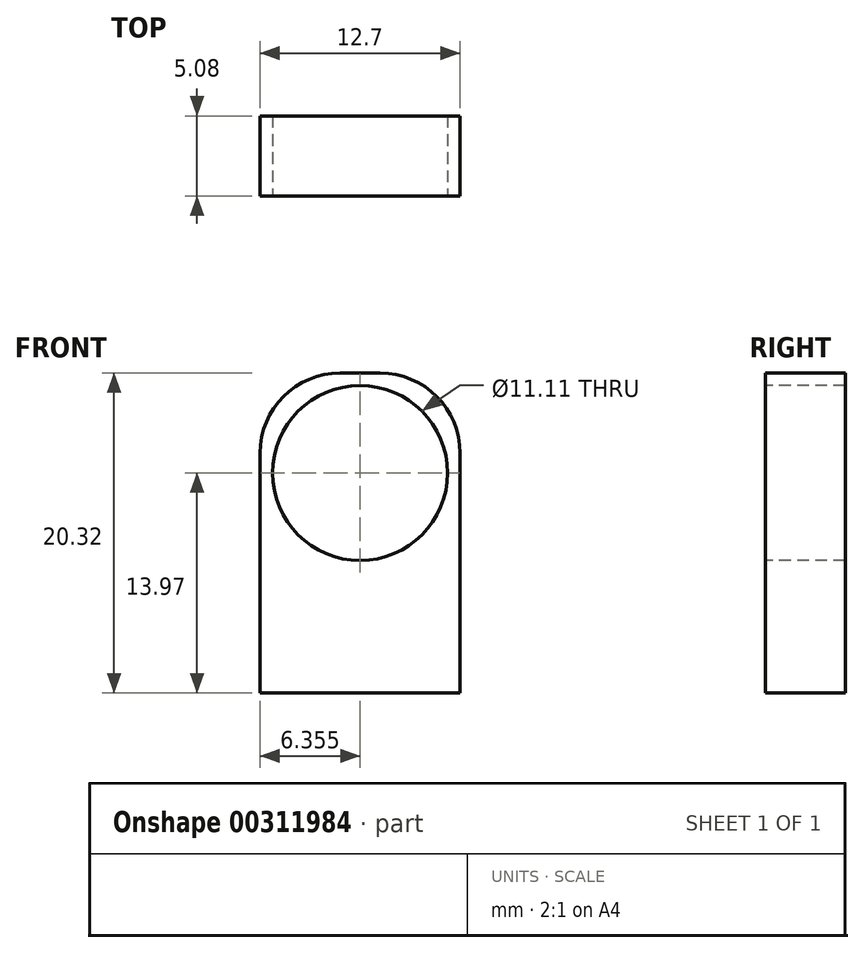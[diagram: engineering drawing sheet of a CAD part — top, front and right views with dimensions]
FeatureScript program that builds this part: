
annotation { "Feature Type Name" : "Feature", "Feature Type Description" : "" }
export const myFeature = defineFeature(function(context is Context, id is Id, definition is map)
    precondition{}
    {
        {
            var Q0;
            Q0=qCreatedBy(makeId("Top.planeOp"),FACE);
            var sketch = newSketch(context, id + "F0", { "sketchPlane" : qUnion([Q0])});
            skLineSegment(sketch, "E0.bottom", {"start": v(-92.4, 61.45) * mm, "end": v(-79.7, 61.45) * mm});
            skLineSegment(sketch, "E0.top", {"start": v(-92.4, 56.37) * mm, "end": v(-79.7, 56.37) * mm});
            skLineSegment(sketch, "E0.left", {"start": v(-92.4, 61.45) * mm, "end": v(-92.4, 56.37) * mm});
            skLineSegment(sketch, "E0.right", {"start": v(-79.7, 61.45) * mm, "end": v(-79.7, 56.37) * mm});
            skSolve(sketch);
        }
        {
            var Q0;
            Q0 = qSketchRegion(id + "F0", true);
            extrude(context, id + "F1", {"entities" : qUnion([Q0]), "depth" : 7.62 * mm});
        }
        {
            var Q0;
            Q0=makeQuery(id+"F1.opExtrude","CAP_FACE",FACE,{"disambiguationData":[OSD([sQuery(id+"F0.wireOp",EDGE,"E0.bottom"),sQuery(id+"F0.wireOp",EDGE,"E0.top"),sQuery(id+"F0.wireOp",EDGE,"E0.left"),sQuery(id+"F0.wireOp",EDGE,"E0.right")])],"isStart":false});
            var sketch = newSketch(context, id + "F2", { "sketchPlane" : qUnion([Q0])});
            skLineSegment(sketch, "E1.bottom", {"start": v(-79.7, 61.45) * mm, "end": v(-92.4, 61.45) * mm});
            skLineSegment(sketch, "E1.top", {"start": v(-79.7, 56.37) * mm, "end": v(-92.4, 56.37) * mm});
            skLineSegment(sketch, "E1.left", {"start": v(-79.7, 61.45) * mm, "end": v(-79.7, 56.37) * mm});
            skLineSegment(sketch, "E1.right", {"start": v(-92.4, 61.45) * mm, "end": v(-92.4, 56.37) * mm});
            skPoint(sketch, "E1.middle", {"position": v(-86.06, 58.9) * mm});
            skPoint(sketch, "E1.middle.positionSnap0", {"position": v(-79.7, 58.9) * mm});
            skPoint(sketch, "E1.middle.positionSnap1", {"position": v(-86.06, 61.45) * mm});
            skPoint(sketch, "E1.centerSnap0", {"position": v(-79.7, 58.9) * mm});
            skPoint(sketch, "E1.centerSnap1", {"position": v(-86.06, 61.45) * mm});
            skSolve(sketch);
        }
        {
            var Q0;
            Q0 = qSketchRegion(id + "F2", true);
            extrude(context, id + "F3", {"entities" : qUnion([Q0]), "operationType" : NewBodyOperationType.ADD, "depth" : 12.7 * mm});
        }
        {
            var Q0;
            Q0=makeQuery(id+"F3.boolean.opBoolean","MERGE",FACE,{"derivedFrom":[makeQuery(id+"F1.opExtrude","SWEPT_FACE",FACE,{"disambiguationData":[OSD([sQuery(id+"F0.wireOp",EDGE,"E0.top")])]}),makeQuery(id+"F3.opExtrude","SWEPT_FACE",FACE,{"disambiguationData":[OSD([sQuery(id+"F2.wireOp",EDGE,"E1.top")])]})]});
            var sketch = newSketch(context, id + "F4", { "sketchPlane" : qUnion([Q0])});
            skCircle(sketch, "E2", {"center": v(-86.06, 13.97) * mm, "radius": 5.56 * mm});
            skPoint(sketch, "E2.centerSnap0", {"position": v(-86.06, 20.32) * mm});
            skSolve(sketch);
        }
        {
            var Q0;
            Q0=makeQuery(id+"F4.imprint","IMPRINT",FACE,{"disambiguationData":[TD([[makeQuery(id+"F4.imprint","IMPRINT",EDGE,{"derivedFrom":sQuery(id+"F4.wireOp",EDGE,"E2")}),1.0]])]});
            extrude(context, id + "F5", {"entities" : qUnion([Q0]), "operationType" : NewBodyOperationType.REMOVE, "oppositeDirection" : true, "depth" : 25.4 * mm});
        }
        {
            var Q0;
            Q0=makeQuery(id+"F3.opExtrude","CAP_EDGE",EDGE,{"disambiguationData":[OSD([sQuery(id+"F2.wireOp",EDGE,"E1.right")])],"isStart":false});
            var Q1;
            Q1=makeQuery(id+"F3.opExtrude","CAP_EDGE",EDGE,{"disambiguationData":[OSD([sQuery(id+"F2.wireOp",EDGE,"E1.left")])],"isStart":false});
            fillet(context, id + "F6", {"entities" : qUnion([Q0, Q1]), "radius" : 5.08 * mm, "tangentPropagation" : true, "allowEdgeOverflow" : false});
        }
    });
